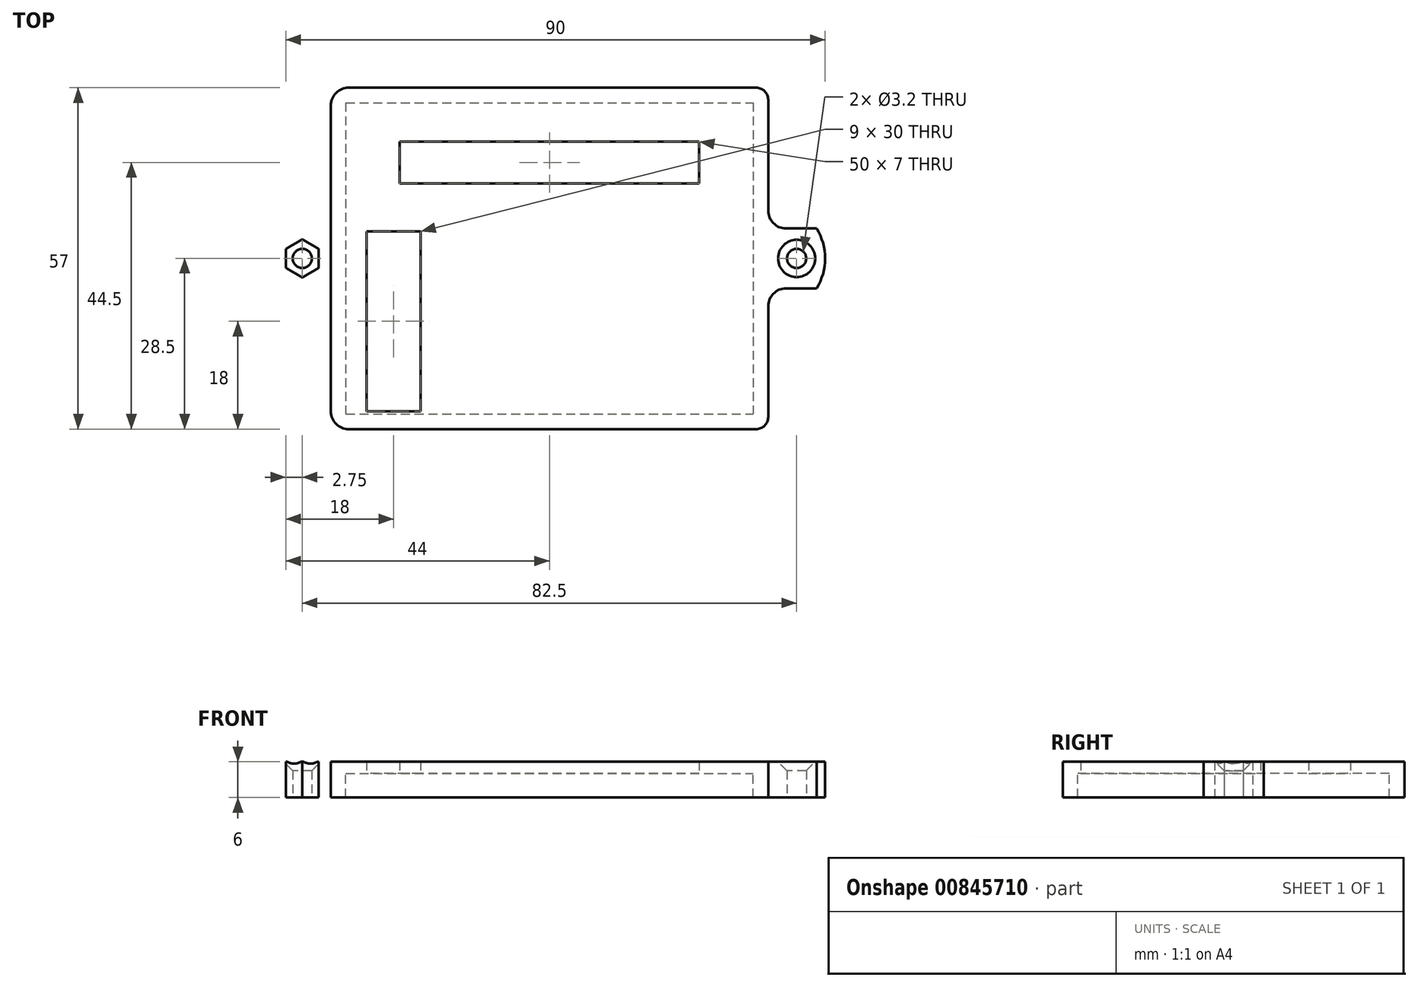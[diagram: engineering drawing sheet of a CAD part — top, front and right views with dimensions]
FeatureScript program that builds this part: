
annotation { "Feature Type Name" : "Feature", "Feature Type Description" : "" }
export const myFeature = defineFeature(function(context is Context, id is Id, definition is map)
    precondition{}
    {
        {
            var Q0;
            Q0=qCreatedBy(makeId("Top.planeOp"),FACE);
            var sketch = newSketch(context, id + "F0", { "sketchPlane" : qUnion([Q0])});
            skLineSegment(sketch, "E0.bottom", {"start": v(-34, 26) * mm, "end": v(-29.05, 26) * mm});
            skLineSegment(sketch, "E0.top", {"start": v(-34, -26) * mm, "end": v(-29.05, -26) * mm});
            skLineSegment(sketch, "E0.left", {"start": v(-34, 26) * mm, "end": v(-34, 21.05) * mm});
            skLineSegment(sketch, "E0.right", {"start": v(34, 26) * mm, "end": v(34, 21.05) * mm});
            skLineSegment(sketch, "E1.0", {"start": v(-36.5, 28.5) * mm, "end": v(-36.5, -28.5) * mm});
            skLineSegment(sketch, "E1.1", {"start": v(-36.5, 28.5) * mm, "end": v(36.5, 28.5) * mm});
            skLineSegment(sketch, "E1.2", {"start": v(36.5, 28.5) * mm, "end": v(36.5, -28.5) * mm});
            skLineSegment(sketch, "E1.3", {"start": v(-36.5, -28.5) * mm, "end": v(36.5, -28.5) * mm});
            skLineSegment(sketch, "E2", {"start": v(-34, 21.05) * mm, "end": v(-29.05, 26) * mm});
            skLineSegment(sketch, "E3", {"start": v(29.05, 26) * mm, "end": v(34, 21.05) * mm});
            skLineSegment(sketch, "E4", {"start": v(34, -21.05) * mm, "end": v(29.05, -26) * mm});
            skLineSegment(sketch, "E5", {"start": v(-34, -21.05) * mm, "end": v(-29.05, -26) * mm});
            skLineSegment(sketch, "E6", {"start": v(-29.05, 26) * mm, "end": v(29.05, 26) * mm});
            skLineSegment(sketch, "E7", {"start": v(-34, 21.05) * mm, "end": v(-34, -21.05) * mm});
            skLineSegment(sketch, "E8", {"start": v(29.05, 26) * mm, "end": v(34, 26) * mm});
            skLineSegment(sketch, "E9", {"start": v(34, 21.05) * mm, "end": v(34, -21.05) * mm});
            skLineSegment(sketch, "E10", {"start": v(29.05, -26) * mm, "end": v(34, -26) * mm});
            skLineSegment(sketch, "E11", {"start": v(34, -21.05) * mm, "end": v(34, -26) * mm});
            skLineSegment(sketch, "E12", {"start": v(-29.05, -26) * mm, "end": v(29.05, -26) * mm});
            skLineSegment(sketch, "E13", {"start": v(-34, -21.05) * mm, "end": v(-34, -26) * mm});
            skLineSegment(sketch, "E14", {"start": v(-36.5, 0) * mm, "end": v(36.5, 0) * mm, "construction": true});
            skArc(sketch, "E15", {"start": v(-44.58, -5) * mm, "mid": v(-46, 0) * mm, "end": v(-44.58, 5) * mm});
            skLineSegment(sketch, "E16", {"start": v(0, 28.5) * mm, "end": v(0, -28.5) * mm, "construction": true});
            skLineSegment(sketch, "E17", {"start": v(-36.5, 0) * mm, "end": v(-46, 0) * mm, "construction": true});
            skCircle(sketch, "E18.cCircle", {"center": v(-41.25, 0) * mm, "radius": 2.75 * mm, "construction": true});
            skLineSegment(sketch, "E18.0", {"start": v(-38.5, -1.59) * mm, "end": v(-41.25, -3.18) * mm});
            skLineSegment(sketch, "E18.1", {"start": v(-41.25, -3.18) * mm, "end": v(-44, -1.59) * mm});
            skLineSegment(sketch, "E18.2", {"start": v(-44, -1.59) * mm, "end": v(-44, 1.59) * mm});
            skLineSegment(sketch, "E18.3", {"start": v(-44, 1.59) * mm, "end": v(-41.25, 3.18) * mm});
            skLineSegment(sketch, "E18.4", {"start": v(-41.25, 3.18) * mm, "end": v(-38.5, 1.59) * mm});
            skLineSegment(sketch, "E18.5", {"start": v(-38.5, 1.59) * mm, "end": v(-38.5, -1.59) * mm});
            skPoint(sketch, "E18.0.midPoint", {"position": v(-39.87, -2.38) * mm});
            skLineSegment(sketch, "E19", {"start": v(-44.58, -5) * mm, "end": v(-36.5, -5) * mm});
            skLineSegment(sketch, "E20", {"start": v(-44.58, 5) * mm, "end": v(-36.5, 5) * mm});
            skLineSegment(sketch, "E21.MirrorCS", {"start": v(38.5, -1.59) * mm, "end": v(41.25, -3.18) * mm});
            skLineSegment(sketch, "E22.MirrorCS", {"start": v(41.25, 3.18) * mm, "end": v(38.5, 1.59) * mm});
            skLineSegment(sketch, "E23.MirrorCS", {"start": v(41.25, -3.18) * mm, "end": v(44, -1.59) * mm});
            skPoint(sketch, "E24.MirrorP", {"position": v(39.87, -2.38) * mm});
            skLineSegment(sketch, "E25.MirrorCS", {"start": v(44, 1.59) * mm, "end": v(41.25, 3.18) * mm});
            skLineSegment(sketch, "E26.MirrorCS", {"start": v(44, -1.59) * mm, "end": v(44, 1.59) * mm});
            skLineSegment(sketch, "E27.MirrorCS", {"start": v(44.58, -5) * mm, "end": v(36.5, -5) * mm});
            skLineSegment(sketch, "E28.MirrorCS", {"start": v(36.5, 0) * mm, "end": v(46, 0) * mm, "construction": true});
            skCircle(sketch, "E29.MirrorC", {"center": v(41.25, 0) * mm, "radius": 2.75 * mm, "construction": true});
            skLineSegment(sketch, "E30.MirrorCS", {"start": v(38.5, 1.59) * mm, "end": v(38.5, -1.59) * mm});
            skLineSegment(sketch, "E31.MirrorCS", {"start": v(44.58, 5) * mm, "end": v(36.5, 5) * mm});
            skArc(sketch, "E32.MirrorCS", {"start": v(44.58, -5) * mm, "mid": v(46, 0) * mm, "end": v(44.58, 5) * mm});
            skCircle(sketch, "E33", {"center": v(-41.25, 0) * mm, "radius": 1.6 * mm});
            skCircle(sketch, "E34", {"center": v(41.25, 0) * mm, "radius": 1.6 * mm});
            skLineSegment(sketch, "E35", {"start": v(-34, 16) * mm, "end": v(34, 16) * mm, "construction": true});
            skLineSegment(sketch, "E36.bottom", {"start": v(25, 12.5) * mm, "end": v(-25, 12.5) * mm});
            skLineSegment(sketch, "E36.top", {"start": v(25, 19.5) * mm, "end": v(-25, 19.5) * mm});
            skLineSegment(sketch, "E36.left", {"start": v(25, 12.5) * mm, "end": v(25, 19.5) * mm});
            skLineSegment(sketch, "E36.right", {"start": v(-25, 12.5) * mm, "end": v(-25, 19.5) * mm});
            skPoint(sketch, "E36.middle", {"position": v(0, 16) * mm});
            skLineSegment(sketch, "E37", {"start": v(-26, 26) * mm, "end": v(-26, -26) * mm, "construction": true});
            skLineSegment(sketch, "E38.bottom", {"start": v(-21.5, -25.5) * mm, "end": v(-30.5, -25.5) * mm});
            skLineSegment(sketch, "E38.top", {"start": v(-21.5, 4.5) * mm, "end": v(-30.5, 4.5) * mm});
            skLineSegment(sketch, "E38.left", {"start": v(-21.5, -25.5) * mm, "end": v(-21.5, 4.5) * mm});
            skLineSegment(sketch, "E38.right", {"start": v(-30.5, -25.5) * mm, "end": v(-30.5, 4.5) * mm});
            skPoint(sketch, "E38.middle", {"position": v(-26, -10.5) * mm});
            skSolve(sketch);
        }
        {
            var Q0;
            Q0=makeQuery(id+"F0.imprint","IMPRINT",FACE,{"disambiguationData":[TD([[makeQuery(id+"F0.imprint","IMPRINT",EDGE,{"derivedFrom":sQuery(id+"F0.wireOp",EDGE,"E15")}),-1.0]])]});
            var Q1;
            Q1=makeQuery(id+"F0.imprint","IMPRINT",FACE,{"disambiguationData":[TD([[makeQuery(id+"F0.imprint","IMPRINT",EDGE,{"derivedFrom":sQuery(id+"F0.wireOp",EDGE,"E0.bottom")}),1.0]])]});
            var Q2;
            Q2=makeQuery(id+"F0.imprint","IMPRINT",FACE,{"disambiguationData":[TD([[makeQuery(id+"F0.imprint","IMPRINT",EDGE,{"derivedFrom":sQuery(id+"F0.wireOp",EDGE,"E2")}),-1.0]])]});
            var Q3;
            Q3=makeQuery(id+"F0.imprint","IMPRINT",FACE,{"disambiguationData":[TD([[makeQuery(id+"F0.imprint","IMPRINT",EDGE,{"derivedFrom":sQuery(id+"F0.wireOp",EDGE,"E21.MirrorCS")}),-1.0]])]});
            var Q4;
            Q4=makeQuery(id+"F0.imprint","IMPRINT",FACE,{"disambiguationData":[TD([[makeQuery(id+"F0.imprint","IMPRINT",EDGE,{"derivedFrom":sQuery(id+"F0.wireOp",EDGE,"E18.0")}),-1.0]])]});
            var Q5;
            Q5=makeQuery(id+"F0.imprint","IMPRINT",FACE,{"disambiguationData":[TD([[makeQuery(id+"F0.imprint","IMPRINT",EDGE,{"derivedFrom":sQuery(id+"F0.wireOp",EDGE,"E21.MirrorCS")}),1.0]])]});
            var Q6;
            Q6=makeQuery(id+"F0.imprint","IMPRINT",FACE,{"disambiguationData":[TD([[makeQuery(id+"F0.imprint","IMPRINT",EDGE,{"derivedFrom":sQuery(id+"F0.wireOp",EDGE,"E0.right")}),-1.0]])]});
            var Q7;
            Q7=makeQuery(id+"F0.imprint","IMPRINT",FACE,{"disambiguationData":[TD([[makeQuery(id+"F0.imprint","IMPRINT",EDGE,{"derivedFrom":sQuery(id+"F0.wireOp",EDGE,"E0.bottom")}),-1.0]])]});
            var Q8;
            Q8=makeQuery(id+"F0.imprint","IMPRINT",FACE,{"disambiguationData":[TD([[makeQuery(id+"F0.imprint","IMPRINT",EDGE,{"derivedFrom":sQuery(id+"F0.wireOp",EDGE,"E0.top")}),1.0]])]});
            var Q9;
            Q9=makeQuery(id+"F0.imprint","IMPRINT",FACE,{"disambiguationData":[TD([[makeQuery(id+"F0.imprint","IMPRINT",EDGE,{"derivedFrom":sQuery(id+"F0.wireOp",EDGE,"E4")}),1.0]])]});
            extrude(context, id + "F1", {"entities" : qUnion([Q0, Q1, Q2, Q3, Q4, Q5, Q6, Q7, Q8, Q9]), "depth" : 2 * mm, "offsetDistance" : 25 * mm});
        }
        {
            var Q0;
            Q0=makeQuery(id+"F0.imprint","IMPRINT",FACE,{"disambiguationData":[TD([[makeQuery(id+"F0.imprint","IMPRINT",EDGE,{"derivedFrom":sQuery(id+"F0.wireOp",EDGE,"E0.bottom")}),1.0]])]});
            var Q1;
            Q1=makeQuery(id+"F0.imprint","IMPRINT",FACE,{"disambiguationData":[TD([[makeQuery(id+"F0.imprint","IMPRINT",EDGE,{"derivedFrom":sQuery(id+"F0.wireOp",EDGE,"E15")}),-1.0]])]});
            var Q2;
            Q2=makeQuery(id+"F0.imprint","IMPRINT",FACE,{"disambiguationData":[TD([[makeQuery(id+"F0.imprint","IMPRINT",EDGE,{"derivedFrom":sQuery(id+"F0.wireOp",EDGE,"E18.0")}),-1.0]])]});
            var Q3;
            Q3=makeQuery(id+"F0.imprint","IMPRINT",FACE,{"disambiguationData":[TD([[makeQuery(id+"F0.imprint","IMPRINT",EDGE,{"derivedFrom":sQuery(id+"F0.wireOp",EDGE,"E21.MirrorCS")}),-1.0]])]});
            var Q4;
            Q4=makeQuery(id+"F0.imprint","IMPRINT",FACE,{"disambiguationData":[TD([[makeQuery(id+"F0.imprint","IMPRINT",EDGE,{"derivedFrom":sQuery(id+"F0.wireOp",EDGE,"E21.MirrorCS")}),1.0]])]});
            extrude(context, id + "F2", {"entities" : qUnion([Q0, Q1, Q2, Q3, Q4]), "operationType" : NewBodyOperationType.ADD, "oppositeDirection" : true, "depth" : 4 * mm, "offsetDistance" : 25 * mm});
        }
        {
            var Q0;
            Q0=makeQuery(id+"F1.opExtrude","CAP_EDGE",EDGE,{"disambiguationData":[OSD([sQuery(id+"F0.wireOp",EDGE,"E33")])],"isStart":false});
            var Q1;
            Q1=makeQuery(id+"F1.opExtrude","CAP_EDGE",EDGE,{"disambiguationData":[OSD([sQuery(id+"F0.wireOp",EDGE,"E34")])],"isStart":false});
            chamfer(context, id + "F3", {"entities" : qUnion([Q0, Q1]), "width" : 1.5 * mm, "tangentPropagation" : true});
        }
        {
            var Q0;
            {var subQ0=sQuery(id+"F0.wireOp",EDGE,"E19");var subQ1=sQuery(id+"F0.wireOp",EDGE,"E1.0");Q0=makeQuery(id+"F2.boolean.opBoolean","MERGE",EDGE,{"derivedFrom":[makeQuery(id+"F1.opExtrude","SWEPT_EDGE",EDGE,{"disambiguationData":[OSD([subQ1,subQ0])]}),makeQuery(id+"F2.opExtrude","SWEPT_EDGE",EDGE,{"disambiguationData":[OSD([subQ1,subQ0])]})]});}
            var Q1;
            {var subQ0=sQuery(id+"F0.wireOp",EDGE,"E20");var subQ1=sQuery(id+"F0.wireOp",EDGE,"E1.0");Q1=makeQuery(id+"F2.boolean.opBoolean","MERGE",EDGE,{"derivedFrom":[makeQuery(id+"F1.opExtrude","SWEPT_EDGE",EDGE,{"disambiguationData":[OSD([subQ1,subQ0])]}),makeQuery(id+"F2.opExtrude","SWEPT_EDGE",EDGE,{"disambiguationData":[OSD([subQ1,subQ0])]})]});}
            var Q2;
            {var subQ0=sQuery(id+"F0.wireOp",EDGE,"E27.MirrorCS");var subQ1=sQuery(id+"F0.wireOp",EDGE,"E1.2");Q2=makeQuery(id+"F2.boolean.opBoolean","MERGE",EDGE,{"derivedFrom":[makeQuery(id+"F1.opExtrude","SWEPT_EDGE",EDGE,{"disambiguationData":[OSD([subQ1,subQ0])]}),makeQuery(id+"F2.opExtrude","SWEPT_EDGE",EDGE,{"disambiguationData":[OSD([subQ1,subQ0])]})]});}
            var Q3;
            {var subQ0=sQuery(id+"F0.wireOp",EDGE,"E31.MirrorCS");var subQ1=sQuery(id+"F0.wireOp",EDGE,"E1.2");Q3=makeQuery(id+"F2.boolean.opBoolean","MERGE",EDGE,{"derivedFrom":[makeQuery(id+"F1.opExtrude","SWEPT_EDGE",EDGE,{"disambiguationData":[OSD([subQ1,subQ0])]}),makeQuery(id+"F2.opExtrude","SWEPT_EDGE",EDGE,{"disambiguationData":[OSD([subQ1,subQ0])]})]});}
            fillet(context, id + "F4", {"entities" : qUnion([Q0, Q1, Q2, Q3]), "radius" : 3 * mm, "tangentPropagation" : true, "allowEdgeOverflow" : false});
        }
        {
            var Q0;
            {var subQ0=sQuery(id+"F0.wireOp",EDGE,"E1.2");var subQ1=sQuery(id+"F0.wireOp",EDGE,"E1.1");Q0=makeQuery(id+"F2.boolean.opBoolean","MERGE",EDGE,{"derivedFrom":[makeQuery(id+"F1.opExtrude","SWEPT_EDGE",EDGE,{"disambiguationData":[OSD([subQ1,subQ0])]}),makeQuery(id+"F2.opExtrude","SWEPT_EDGE",EDGE,{"disambiguationData":[OSD([subQ1,subQ0])]})]});}
            var Q1;
            {var subQ0=sQuery(id+"F0.wireOp",EDGE,"E1.1");var subQ1=sQuery(id+"F0.wireOp",EDGE,"E1.0");Q1=makeQuery(id+"F2.boolean.opBoolean","MERGE",EDGE,{"derivedFrom":[makeQuery(id+"F1.opExtrude","SWEPT_EDGE",EDGE,{"disambiguationData":[OSD([subQ1,subQ0])]}),makeQuery(id+"F2.opExtrude","SWEPT_EDGE",EDGE,{"disambiguationData":[OSD([subQ1,subQ0])]})]});}
            var Q2;
            {var subQ0=sQuery(id+"F0.wireOp",EDGE,"E1.3");var subQ1=sQuery(id+"F0.wireOp",EDGE,"E1.0");Q2=makeQuery(id+"F2.boolean.opBoolean","MERGE",EDGE,{"derivedFrom":[makeQuery(id+"F1.opExtrude","SWEPT_EDGE",EDGE,{"disambiguationData":[OSD([subQ1,subQ0])]}),makeQuery(id+"F2.opExtrude","SWEPT_EDGE",EDGE,{"disambiguationData":[OSD([subQ1,subQ0])]})]});}
            var Q3;
            {var subQ0=sQuery(id+"F0.wireOp",EDGE,"E1.3");var subQ1=sQuery(id+"F0.wireOp",EDGE,"E1.2");Q3=makeQuery(id+"F2.boolean.opBoolean","MERGE",EDGE,{"derivedFrom":[makeQuery(id+"F1.opExtrude","SWEPT_EDGE",EDGE,{"disambiguationData":[OSD([subQ1,subQ0])]}),makeQuery(id+"F2.opExtrude","SWEPT_EDGE",EDGE,{"disambiguationData":[OSD([subQ1,subQ0])]})]});}
            fillet(context, id + "F5", {"entities" : qUnion([Q0, Q1, Q2, Q3]), "radius" : 2 * mm, "tangentPropagation" : true, "allowEdgeOverflow" : false});
        }
    });
